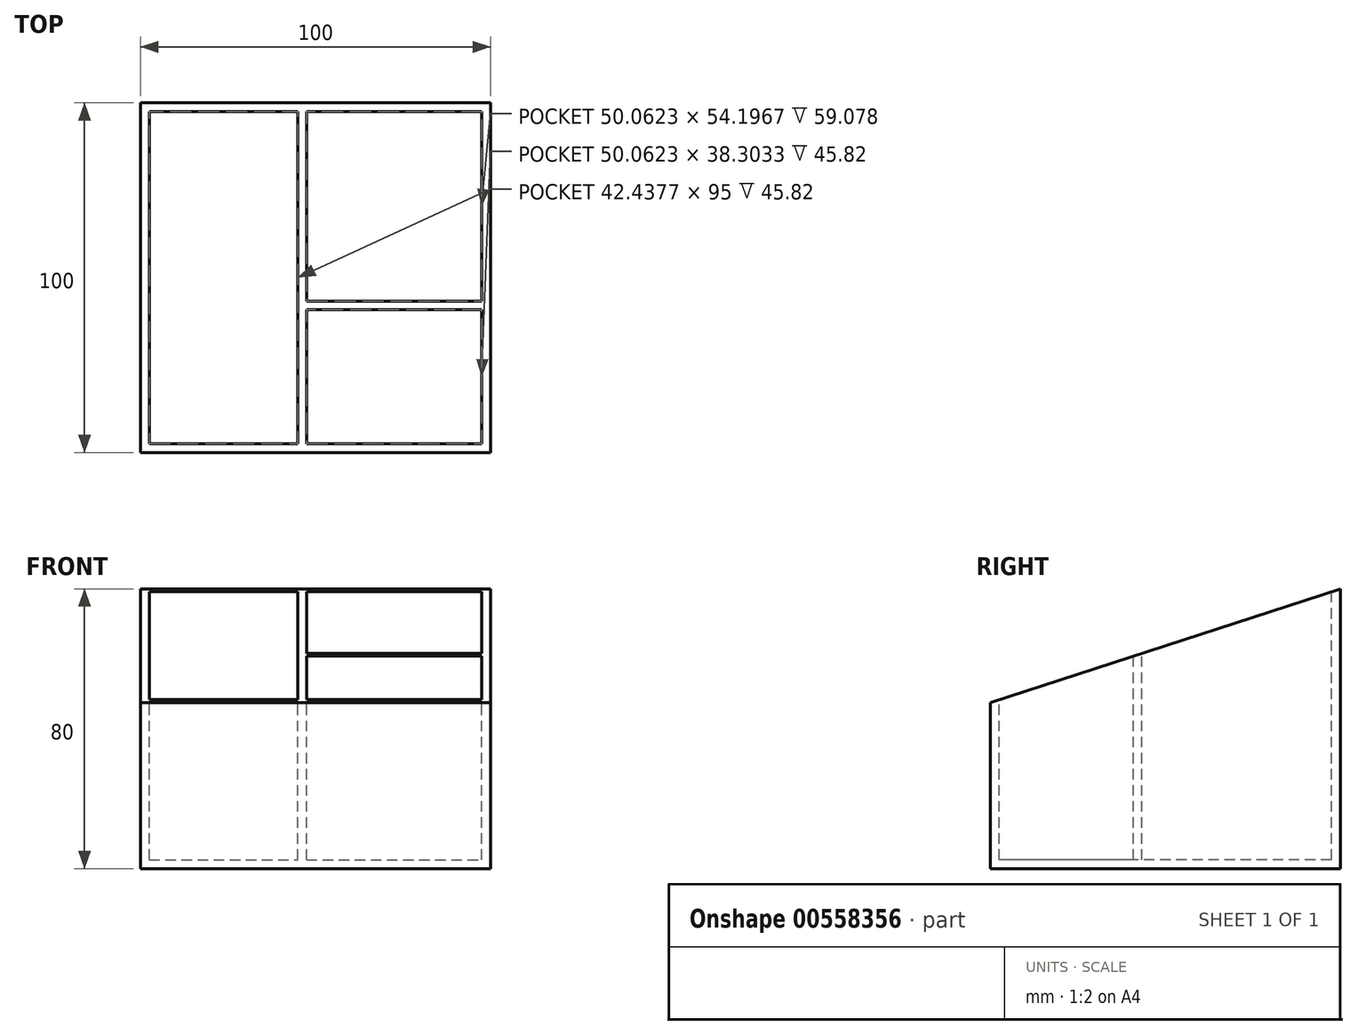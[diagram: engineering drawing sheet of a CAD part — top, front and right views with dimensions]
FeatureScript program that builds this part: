
annotation { "Feature Type Name" : "Feature", "Feature Type Description" : "" }
export const myFeature = defineFeature(function(context is Context, id is Id, definition is map)
    precondition{}
    {
        {
            var Q0;
            Q0=qCreatedBy(makeId("Top.planeOp"),FACE);
            var sketch = newSketch(context, id + "F0", { "sketchPlane" : qUnion([Q0])});
            skLineSegment(sketch, "E0.bottom", {"start": v(-47.44, 56.7) * mm, "end": v(52.56, 56.7) * mm});
            skLineSegment(sketch, "E0.top", {"start": v(-47.44, -43.3) * mm, "end": v(52.56, -43.3) * mm});
            skLineSegment(sketch, "E0.left", {"start": v(-47.44, 56.7) * mm, "end": v(-47.44, -43.3) * mm});
            skLineSegment(sketch, "E0.right", {"start": v(52.56, 56.7) * mm, "end": v(52.56, -43.3) * mm});
            skSolve(sketch);
        }
        {
            var Q0;
            Q0=makeQuery(id+"F0.imprint","IMPRINT",FACE,{"disambiguationData":[TD([[makeQuery(id+"F0.imprint","IMPRINT",EDGE,{"derivedFrom":sQuery(id+"F0.wireOp",EDGE,"E0.bottom")}),-1.0]])]});
            extrude(context, id + "F1", {"entities" : qUnion([Q0]), "depth" : 80 * mm, "offsetDistance" : 25 * mm});
        }
        {
            var Q0;
            Q0=makeQuery(id+"F1.opExtrude","CAP_FACE",FACE,{"disambiguationData":[OSD([sQuery(id+"F0.wireOp",EDGE,"E0.bottom"),sQuery(id+"F0.wireOp",EDGE,"E0.top"),sQuery(id+"F0.wireOp",EDGE,"E0.left"),sQuery(id+"F0.wireOp",EDGE,"E0.right")])],"isStart":false});
            var sketch = newSketch(context, id + "F2", { "sketchPlane" : qUnion([Q0])});
            skLineSegment(sketch, "E1.bottom", {"start": v(-44.94, 54.2) * mm, "end": v(-2.5, 54.2) * mm});
            skLineSegment(sketch, "E1.top", {"start": v(-44.94, -40.8) * mm, "end": v(-2.5, -40.8) * mm});
            skLineSegment(sketch, "E1.left", {"start": v(-44.94, 54.2) * mm, "end": v(-44.94, -40.8) * mm});
            skLineSegment(sketch, "E1.right", {"start": v(-2.5, 54.2) * mm, "end": v(-2.5, -40.8) * mm});
            skLineSegment(sketch, "E2.bottom", {"start": v(0, 54.2) * mm, "end": v(50.06, 54.2) * mm});
            skLineSegment(sketch, "E2.top", {"start": v(0, 0) * mm, "end": v(50.06, 0) * mm});
            skLineSegment(sketch, "E2.left", {"start": v(0, 54.2) * mm, "end": v(0, 0) * mm});
            skLineSegment(sketch, "E2.right", {"start": v(50.06, 54.2) * mm, "end": v(50.06, 0) * mm});
            skLineSegment(sketch, "E3.bottom", {"start": v(0, -2.5) * mm, "end": v(50.06, -2.5) * mm});
            skLineSegment(sketch, "E3.top", {"start": v(0, -40.8) * mm, "end": v(50.06, -40.8) * mm});
            skLineSegment(sketch, "E3.left", {"start": v(0, -2.5) * mm, "end": v(0, -40.8) * mm});
            skLineSegment(sketch, "E3.right", {"start": v(50.06, -2.5) * mm, "end": v(50.06, -40.8) * mm});
            skSolve(sketch);
        }
        {
            var Q0;
            Q0=makeQuery(id+"F2.imprint","IMPRINT",FACE,{"disambiguationData":[TD([[makeQuery(id+"F2.imprint","IMPRINT",EDGE,{"derivedFrom":sQuery(id+"F2.wireOp",EDGE,"E1.bottom")}),-1.0]])]});
            var Q1;
            Q1=makeQuery(id+"F2.imprint","IMPRINT",FACE,{"disambiguationData":[TD([[makeQuery(id+"F2.imprint","IMPRINT",EDGE,{"derivedFrom":sQuery(id+"F2.wireOp",EDGE,"E2.bottom")}),-1.0]])]});
            var Q2;
            Q2=makeQuery(id+"F2.imprint","IMPRINT",FACE,{"disambiguationData":[TD([[makeQuery(id+"F2.imprint","IMPRINT",EDGE,{"derivedFrom":sQuery(id+"F2.wireOp",EDGE,"E3.bottom")}),-1.0]])]});
            extrude(context, id + "F3", {"entities" : qUnion([Q0, Q1, Q2]), "operationType" : NewBodyOperationType.REMOVE, "oppositeDirection" : true, "depth" : 77.5 * mm, "offsetDistance" : 25 * mm});
        }
        {
            var Q0;
            Q0=makeQuery(id+"F1.opExtrude","SWEPT_FACE",FACE,{"disambiguationData":[OSD([sQuery(id+"F0.wireOp",EDGE,"E0.left")])]});
            var sketch = newSketch(context, id + "F4", { "sketchPlane" : qUnion([Q0])});
            skLineSegment(sketch, "E4", {"start": v(-56.7, 80) * mm, "end": v(43.3, 47.5) * mm});
            skSolve(sketch);
        }
        {
            var Q0;
            {var subQ0=sQuery(id+"F4.wireOp",EDGE,"E4");Q0=makeQuery(id+"F4.imprint","IMPRINT",FACE,{"disambiguationData":[TD([[makeQuery(id+"F4.imprint","IMPRINT",EDGE,{"derivedFrom":subQ0}),1.0]])]});}
            extrude(context, id + "F5", {"entities" : qUnion([Q0]), "operationType" : NewBodyOperationType.REMOVE, "oppositeDirection" : true, "depth" : 100 * mm, "offsetDistance" : 25 * mm});
        }
    });
